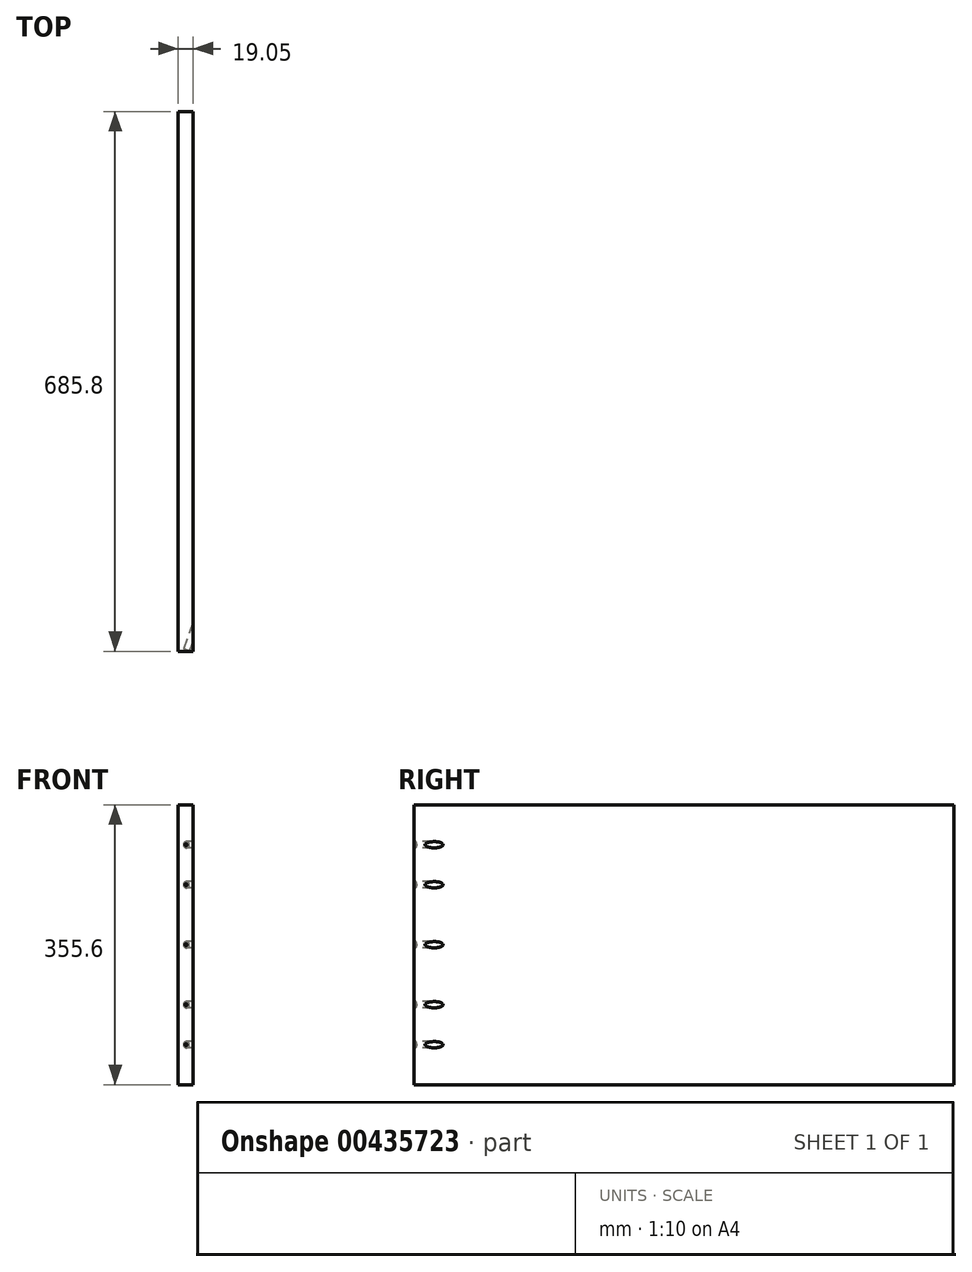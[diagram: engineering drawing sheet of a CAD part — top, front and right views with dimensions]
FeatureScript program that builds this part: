
annotation { "Feature Type Name" : "Feature", "Feature Type Description" : "" }
export const myFeature = defineFeature(function(context is Context, id is Id, definition is map)
    precondition{}
    {
        {
            var Q0;
            Q0=qCreatedBy(makeId("Right.planeOp"),FACE);
            var sketch = newSketch(context, id + "F0", { "sketchPlane" : qUnion([Q0])});
            skLineSegment(sketch, "E0.bottom", {"start": v(342.9, -177.8) * mm, "end": v(-342.9, -177.8) * mm});
            skLineSegment(sketch, "E0.top", {"start": v(342.9, 177.8) * mm, "end": v(-342.9, 177.8) * mm});
            skLineSegment(sketch, "E0.left", {"start": v(342.9, -177.8) * mm, "end": v(342.9, 177.8) * mm});
            skLineSegment(sketch, "E0.right", {"start": v(-342.9, -177.8) * mm, "end": v(-342.9, 177.8) * mm});
            skPoint(sketch, "E0.middle", {"position": v(0, 0) * mm});
            skSolve(sketch);
        }
        {
            var Q0;
            Q0=makeQuery(id+"F0.imprint","IMPRINT",FACE,{"disambiguationData":[TD([[makeQuery(id+"F0.imprint","IMPRINT",EDGE,{"derivedFrom":sQuery(id+"F0.wireOp",EDGE,"E0.bottom")}),-1.0]])]});
            extrude(context, id + "F1", {"entities" : qUnion([Q0]), "depth" : 19.05 * mm});
        }
        {
            var Q0;
            Q0=makeQuery(id+"F1.opExtrude","SWEPT_FACE",FACE,{"disambiguationData":[OSD([sQuery(id+"F0.wireOp",EDGE,"E0.right")])]});
            cPlane(context, id + "F2", {"entities" : qUnion([Q0]), "cplaneType" : CPlaneType.OFFSET, "offset" : 25.4 * mm, "oppositeDirection" : true, "width" : 152.4 * mm, "height" : 152.4 * mm});
        }
        {
            var Q0;
            Q0=qCreatedBy(id+"F2.planeOp",FACE);
            var sketch = newSketch(context, id + "F3", { "sketchPlane" : qUnion([Q0])});
            skLineSegment(sketch, "E1.0", {"start": v(19.05, -177.8) * mm, "end": v(19.05, 177.8) * mm});
            skSolve(sketch);
        }
        {
            var Q0;
            Q0=sQuery(id+"F3.wireOp",EDGE,"E1.0");
            var Q1;
            Q1=makeQuery(id+"F1.opExtrude","CAP_FACE",FACE,{"disambiguationData":[OSD([sQuery(id+"F0.wireOp",EDGE,"E0.bottom"),sQuery(id+"F0.wireOp",EDGE,"E0.top"),sQuery(id+"F0.wireOp",EDGE,"E0.left"),sQuery(id+"F0.wireOp",EDGE,"E0.right")])],"isStart":false});
            cPlane(context, id + "F4", {"entities" : qUnion([Q0, Q1]), "cplaneType" : CPlaneType.LINE_ANGLE, "offset" : 25.4 * mm, "angle" : 70 * degree, "width" : 152.4 * mm, "height" : 152.4 * mm});
        }
        {
            var Q0;
            Q0=qCreatedBy(id+"F4.planeOp",FACE);
            var sketch = newSketch(context, id + "F5", { "sketchPlane" : qUnion([Q0])});
            skLineSegment(sketch, "E2.0", {"start": v(126.5, -177.8) * mm, "end": v(126.5, 177.8) * mm});
            skCircle(sketch, "E3", {"center": v(126.5, -127) * mm, "radius": 3.94 * mm});
            skCircle(sketch, "E4", {"center": v(126.5, -76.2) * mm, "radius": 3.94 * mm});
            skCircle(sketch, "E5", {"center": v(126.5, 0) * mm, "radius": 3.94 * mm});
            skCircle(sketch, "E6", {"center": v(126.5, 76.2) * mm, "radius": 3.94 * mm});
            skCircle(sketch, "E7", {"center": v(126.5, 127) * mm, "radius": 3.94 * mm});
            skSolve(sketch);
        }
        {
            var Q0;
            Q0 = qSketchRegion(id + "F5", true);
            extrude(context, id + "F6", {"entities" : qUnion([Q0]), "operationType" : NewBodyOperationType.REMOVE, "endBound" : BoundingType.SYMMETRIC, "oppositeDirection" : true, "depth" : 50.8 * mm});
        }
        {
            var Q0;
            Q0=makeQuery(id+"F6.boolean.opBoolean","COPY",FACE,{"derivedFrom":makeQuery(id+"F6.opExtrude","CAP_FACE",FACE,{"disambiguationData":[OSD([sQuery(id+"F5.wireOp",EDGE,"E3")])],"isStart":true})});
            var sketch = newSketch(context, id + "F7", { "sketchPlane" : qUnion([Q0])});
            skCircle(sketch, "E8.0", {"center": v(-126.5, -127) * mm, "radius": 3.94 * mm});
            skCircle(sketch, "E9.0", {"center": v(-126.5, -76.2) * mm, "radius": 3.94 * mm});
            skCircle(sketch, "E10.0", {"center": v(-126.5, 0) * mm, "radius": 3.94 * mm});
            skCircle(sketch, "E11.0", {"center": v(-126.5, 76.2) * mm, "radius": 3.94 * mm});
            skCircle(sketch, "E12.0", {"center": v(-126.5, 127) * mm, "radius": 3.94 * mm});
            skSolve(sketch);
        }
        {
            var Q0;
            Q0=sQuery(id+"F7.wireOp",VERTEX,"E12.0.center");
            var Q1;
            Q1=sQuery(id+"F7.wireOp",VERTEX,"E11.0.center");
            var Q2;
            Q2=sQuery(id+"F7.wireOp",VERTEX,"E10.0.center");
            var Q3;
            Q3=sQuery(id+"F7.wireOp",VERTEX,"E9.0.center");
            var Q4;
            Q4=sQuery(id+"F7.wireOp",VERTEX,"E8.0.center");
            var Q5;
            Q5=makeQuery(id+"F1.opExtrude","SWEPT_BODY",BODY,{"disambiguationData":[OSD([sQuery(id+"F0.wireOp",EDGE,"E0.bottom"),sQuery(id+"F0.wireOp",EDGE,"E0.top"),sQuery(id+"F0.wireOp",EDGE,"E0.left"),sQuery(id+"F0.wireOp",EDGE,"E0.right")])]});
            hole(context, id + "F8", {"style" : HoleStyle.SIMPLE, "endStyle" : HoleEndStyle.THROUGH, "holeDiameter" : 2.54 * mm, "isTappedThrough" : true, "tappedDepth" : 12.7 * mm, "tapClearance" : 3, "locations" : qUnion([Q0, Q1, Q2, Q3, Q4]), "scope" : qUnion([Q5])});
        }
    });
